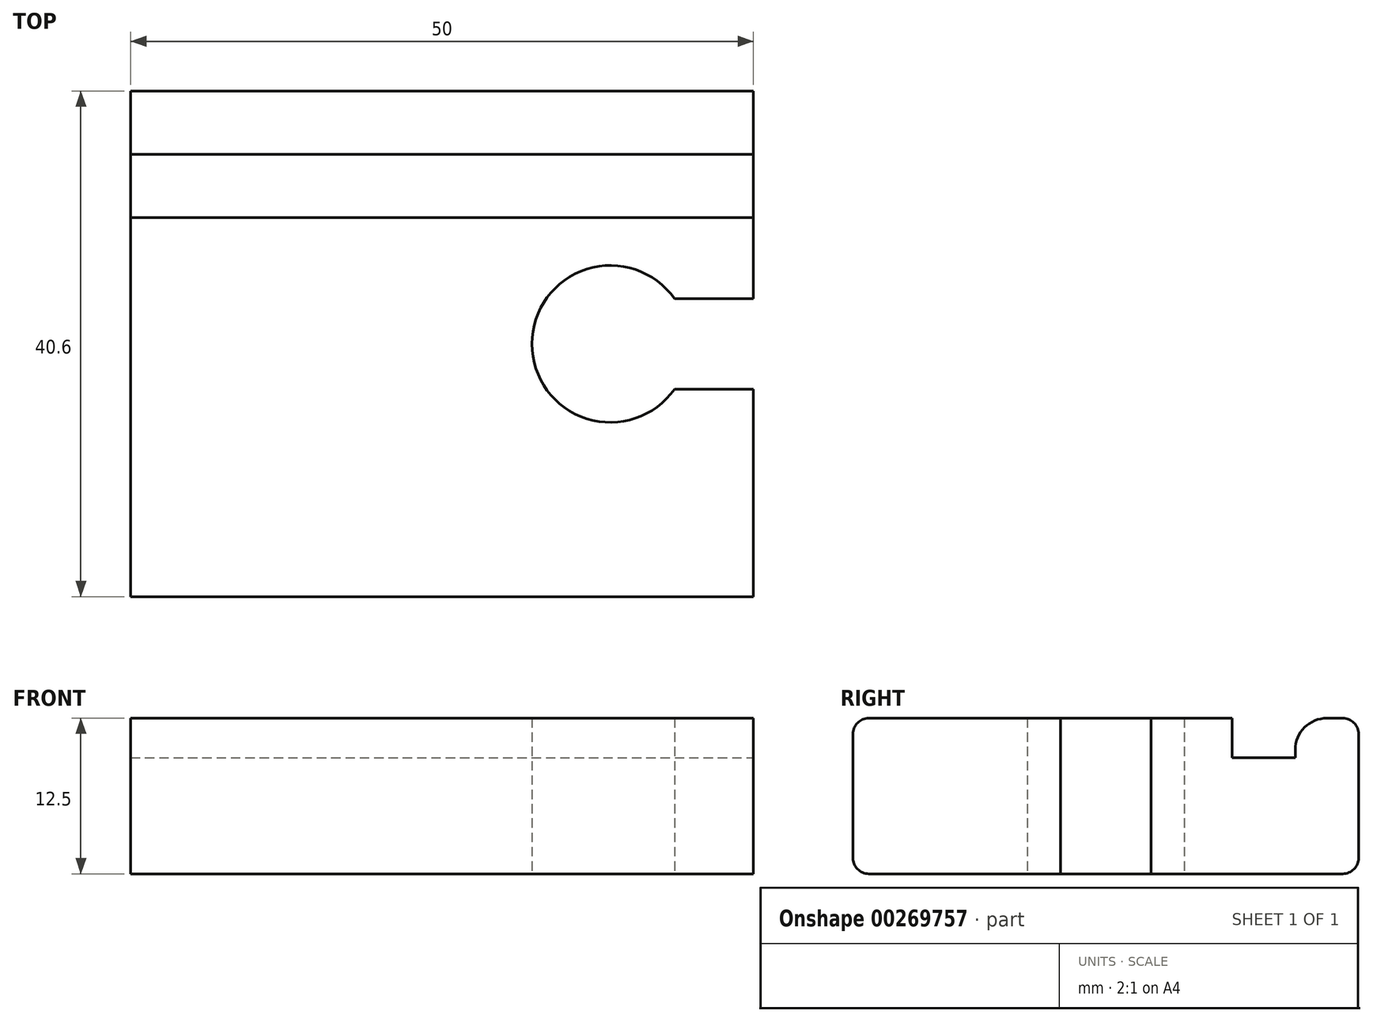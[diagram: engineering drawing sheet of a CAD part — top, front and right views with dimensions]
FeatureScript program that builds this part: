
annotation { "Feature Type Name" : "Feature", "Feature Type Description" : "" }
export const myFeature = defineFeature(function(context is Context, id is Id, definition is map)
    precondition{}
    {
        {
            var Q0;
            Q0=qCreatedBy(makeId("Top.planeOp"),FACE);
            var sketch = newSketch(context, id + "F0", { "sketchPlane" : qUnion([Q0])});
            skLineSegment(sketch, "E0.bottom", {"start": v(25, 20.3) * mm, "end": v(-25, 20.3) * mm});
            skLineSegment(sketch, "E0.top", {"start": v(25, -20.3) * mm, "end": v(-25, -20.3) * mm});
            skLineSegment(sketch, "E0.left", {"start": v(25, 20.3) * mm, "end": v(25, -20.3) * mm});
            skLineSegment(sketch, "E0.right", {"start": v(-25, 20.3) * mm, "end": v(-25, -20.3) * mm});
            skPoint(sketch, "E0.middle", {"position": v(0, 0) * mm});
            skSolve(sketch);
        }
        {
            var Q0;
            Q0=qSketchRegion(id+"F0",true);
            extrude(context, id + "F1", {"entities" : qUnion([Q0]), "depth" : 12.5 * mm});
        }
        {
            var Q0;
            Q0=qCreatedBy(makeId("Top.planeOp"),FACE);
            var sketch = newSketch(context, id + "F2", { "sketchPlane" : qUnion([Q0])});
            skLineSegment(sketch, "E1.right", {"start": v(25, 3.62) * mm, "end": v(25, -2.8) * mm});
            skLineSegment(sketch, "E2", {"start": v(25, 0) * mm, "end": v(13.52, 0) * mm, "construction": true});
            skArc(sketch, "E3", {"start": v(18.67, 3.62) * mm, "mid": v(7.22, 0) * mm, "end": v(18.67, -3.62) * mm});
            skLineSegment(sketch, "E4.bottom", {"start": v(18.67, 3.62) * mm, "end": v(25, 3.62) * mm});
            skLineSegment(sketch, "E4.top", {"start": v(18.67, -3.62) * mm, "end": v(25, -3.62) * mm});
            skLineSegment(sketch, "E4.right", {"start": v(25, 3.62) * mm, "end": v(25, -3.63) * mm});
            skSolve(sketch);
        }
        {
            var Q0;
            Q0=qSketchRegion(id+"F2",true);
            extrude(context, id + "F3", {"entities" : qUnion([Q0]), "operationType" : NewBodyOperationType.REMOVE, "endBound" : BoundingType.THROUGH_ALL, "depth" : 12 * mm});
        }
        {
            var Q0;
            {var subQ0=sQuery(id+"F2.wireOp",EDGE,"E1.right");var subQ1=sQuery(id+"F2.wireOp",EDGE,"E1.top");var subQ2=sQuery(id+"F2.wireOp",EDGE,"E1.bottom");var subQ3=sQuery(id+"F2.wireOp",EDGE,"Drm0USrt-R8gS-Y0M4-SWiu-MueqH25JkZSp");Q0=makeQuery(id+"Fgbf0bgwTR2DJ2I_1.1.F3.boolean.opBoolean","MERGE",FACE,{"derivedFrom":[makeQuery(id+"F3.boolean.opBoolean","MERGE",FACE,{"derivedFrom":[makeQuery(id+"F1.opExtrude","CAP_FACE",FACE,{"disambiguationData":[OSD([sQuery(id+"F0.wireOp",EDGE,"E0.bottom"),sQuery(id+"F0.wireOp",EDGE,"E0.top"),sQuery(id+"F0.wireOp",EDGE,"E0.left"),sQuery(id+"F0.wireOp",EDGE,"E0.right")])],"isStart":false}),makeQuery(id+"F3.opExtrude","CAP_FACE",FACE,{"disambiguationData":[OSD([subQ3,subQ2,subQ1,subQ0])],"isStart":false})]}),makeQuery(id+"Fgbf0bgwTR2DJ2I_1.1.F3.opExtrude","CAP_FACE",FACE,{"disambiguationData":[OSD([subQ3,subQ2,subQ1,subQ0])],"isStart":false})]});}
            var sketch = newSketch(context, id + "F4", { "sketchPlane" : qUnion([Q0])});
            skLineSegment(sketch, "E5.bottom", {"start": v(-25, 15.22) * mm, "end": v(25, 15.22) * mm});
            skLineSegment(sketch, "E5.top", {"start": v(-25, 10.14) * mm, "end": v(25, 10.14) * mm});
            skLineSegment(sketch, "E5.left", {"start": v(-25, 15.22) * mm, "end": v(-25, 10.14) * mm});
            skLineSegment(sketch, "E5.right", {"start": v(25, 15.22) * mm, "end": v(25, 10.14) * mm});
            skSolve(sketch);
        }
        {
            var Q0;
            Q0=qSketchRegion(id+"F4",true);
            extrude(context, id + "F5", {"entities" : qUnion([Q0]), "operationType" : NewBodyOperationType.REMOVE, "oppositeDirection" : true, "depth" : 3.17 * mm});
        }
        {
            var Q0;
            Q0=makeQuery(id+"F1.opExtrude","CAP_EDGE",EDGE,{"disambiguationData":[OSD([sQuery(id+"F0.wireOp",EDGE,"E0.bottom")])],"isStart":false});
            var Q1;
            Q1=makeQuery(id+"F1.opExtrude","CAP_EDGE",EDGE,{"disambiguationData":[OSD([sQuery(id+"F0.wireOp",EDGE,"E0.top")])],"isStart":false});
            var Q2;
            Q2=makeQuery(id+"F1.opExtrude","CAP_EDGE",EDGE,{"disambiguationData":[OSD([sQuery(id+"F0.wireOp",EDGE,"E0.bottom")])],"isStart":true});
            var Q3;
            Q3=makeQuery(id+"F1.opExtrude","CAP_EDGE",EDGE,{"disambiguationData":[OSD([sQuery(id+"F0.wireOp",EDGE,"E0.top")])],"isStart":true});
            fillet(context, id + "F6", {"entities" : qUnion([Q0, Q1, Q2, Q3]), "radius" : 1.27 * mm, "tangentPropagation" : true, "allowEdgeOverflow" : false});
        }
        {
            var Q0;
            Q0=makeQuery(id+"F5.boolean.opBoolean","COPY",EDGE,{"derivedFrom":makeQuery(id+"F5.opExtrude","CAP_EDGE",EDGE,{"disambiguationData":[OSD([sQuery(id+"F4.wireOp",EDGE,"E5.bottom")])],"isStart":true})});
            var Q1;
            Q1=makeQuery(id+"F5.boolean.opBoolean","COPY",EDGE,{"derivedFrom":makeQuery(id+"F5.opExtrude","CAP_EDGE",EDGE,{"disambiguationData":[OSD([sQuery(id+"F4.wireOp",EDGE,"E5.top")])],"isStart":true})});
            fillet(context, id + "F7", {"entities" : qUnion([Q0, Q1]), "radius" : 2.54 * mm, "tangentPropagation" : true, "allowEdgeOverflow" : false});
        }
    });
